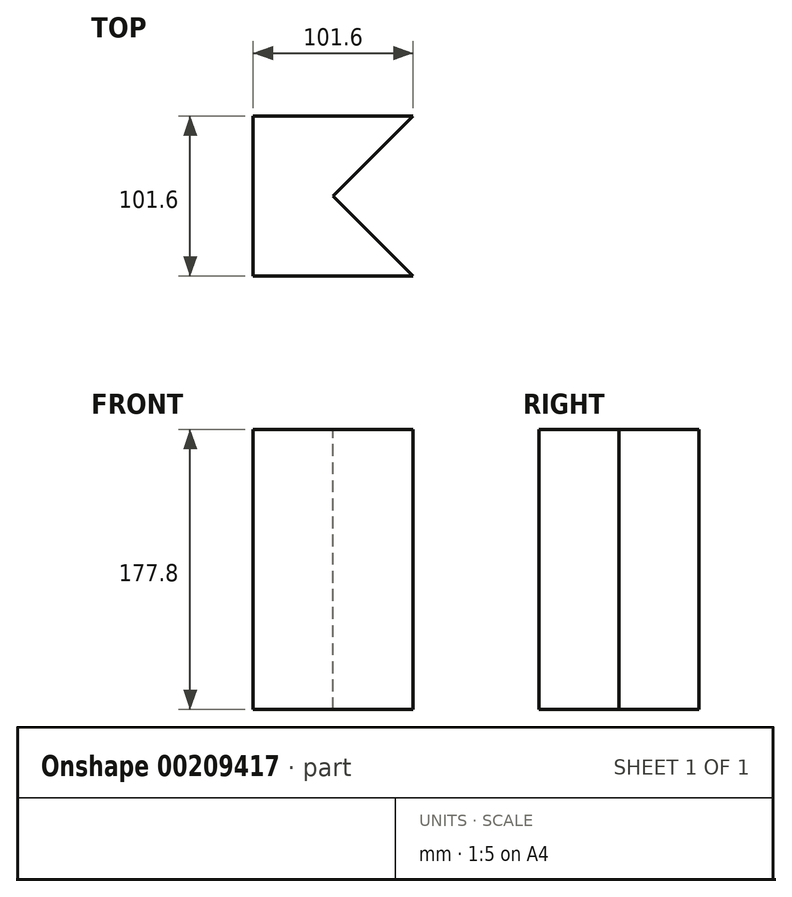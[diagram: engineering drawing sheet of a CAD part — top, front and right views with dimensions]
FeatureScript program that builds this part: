
annotation { "Feature Type Name" : "Feature", "Feature Type Description" : "" }
export const myFeature = defineFeature(function(context is Context, id is Id, definition is map)
    precondition{}
    {
        {
            var Q0;
            Q0=qCreatedBy(makeId("Top.planeOp"),FACE);
            var sketch = newSketch(context, id + "F0", { "sketchPlane" : qUnion([Q0])});
            skLineSegment(sketch, "E0.bottom", {"start": v(-50.8, -50.8) * mm, "end": v(50.8, -50.8) * mm});
            skLineSegment(sketch, "E0.top", {"start": v(-50.8, 50.8) * mm, "end": v(50.8, 50.8) * mm});
            skLineSegment(sketch, "E0.left", {"start": v(-50.8, -50.8) * mm, "end": v(-50.8, 50.8) * mm});
            skLineSegment(sketch, "E0.right", {"start": v(50.8, -50.8) * mm, "end": v(50.8, 50.8) * mm});
            skPoint(sketch, "E0.middle", {"position": v(0, 0) * mm});
            skSolve(sketch);
        }
        {
            var Q0;
            Q0=makeQuery(id+"F0.imprint","IMPRINT",FACE,{"disambiguationData":[TD([[makeQuery(id+"F0.imprint","IMPRINT",EDGE,{"derivedFrom":sQuery(id+"F0.wireOp",EDGE,"E0.bottom")}),1.0]])]});
            extrude(context, id + "F1", {"entities" : qUnion([Q0]), "depth" : 177.8 * mm});
        }
        {
            var Q0;
            Q0=makeQuery(id+"F1.opExtrude","CAP_FACE",FACE,{"disambiguationData":[OSD([sQuery(id+"F0.wireOp",EDGE,"E0.bottom"),sQuery(id+"F0.wireOp",EDGE,"E0.top"),sQuery(id+"F0.wireOp",EDGE,"E0.left"),sQuery(id+"F0.wireOp",EDGE,"E0.right")])],"isStart":false});
            var sketch = newSketch(context, id + "F2", { "sketchPlane" : qUnion([Q0])});
            skLineSegment(sketch, "E1", {"start": v(0, 0) * mm, "end": v(50.8, 50.8) * mm});
            skLineSegment(sketch, "E2", {"start": v(50.8, 50.8) * mm, "end": v(50.8, -50.8) * mm});
            skLineSegment(sketch, "E3", {"start": v(50.8, -50.8) * mm, "end": v(0, 0) * mm});
            skSolve(sketch);
        }
        {
            var Q0;
            Q0 = qSketchRegion(id + "F2", true);
            extrude(context, id + "F3", {"entities" : qUnion([Q0]), "operationType" : NewBodyOperationType.REMOVE, "endBound" : BoundingType.UP_TO_NEXT, "oppositeDirection" : true, "depth" : 25.4 * mm});
        }
    });
